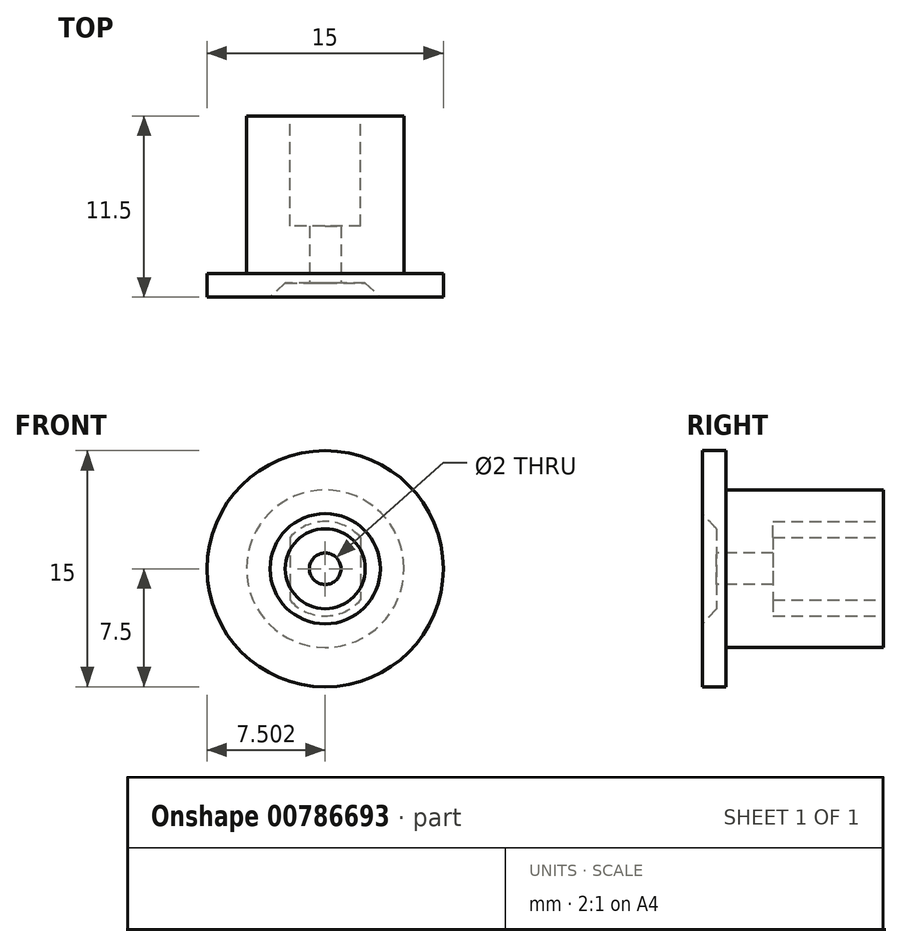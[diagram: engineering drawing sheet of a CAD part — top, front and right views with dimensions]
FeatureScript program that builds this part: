
annotation { "Feature Type Name" : "Feature", "Feature Type Description" : "" }
export const myFeature = defineFeature(function(context is Context, id is Id, definition is map)
    precondition{}
    {
        {
            var Q0;
            Q0=qCreatedBy(makeId("Top.planeOp"),FACE);
            var sketch = newSketch(context, id + "F0", { "sketchPlane" : qUnion([Q0])});
            skLineSegment(sketch, "E0", {"start": v(-45.82, -22.8) * mm, "end": v(-45.82, -33.4) * mm});
            skLineSegment(sketch, "E1", {"start": v(-45.82, -33.4) * mm, "end": v(-48.36, -33.4) * mm});
            skLineSegment(sketch, "E2", {"start": v(-48.36, -33.4) * mm, "end": v(-49.32, -34.3) * mm});
            skLineSegment(sketch, "E3", {"start": v(-49.32, -34.3) * mm, "end": v(-53.32, -34.3) * mm});
            skLineSegment(sketch, "E4", {"start": v(-53.32, -34.3) * mm, "end": v(-53.32, -32.8) * mm});
            skLineSegment(sketch, "E5", {"start": v(-53.32, -32.8) * mm, "end": v(-50.82, -32.8) * mm});
            skLineSegment(sketch, "E6", {"start": v(-50.82, -32.8) * mm, "end": v(-50.82, -22.8) * mm});
            skLineSegment(sketch, "E7", {"start": v(-50.82, -22.8) * mm, "end": v(-45.82, -22.8) * mm});
            skSolve(sketch);
        }
        {
            var Q0;
            Q0=makeQuery(id+"F0.imprint","IMPRINT",FACE,{"disambiguationData":[TD([[makeQuery(id+"F0.imprint","IMPRINT",EDGE,{"derivedFrom":sQuery(id+"F0.wireOp",EDGE,"E0")}),-1.0]])]});
            var Q1;
            Q1=sQuery(id+"F0.wireOp",EDGE,"E0");
            revolve(context, id + "F1", {"surfaceOperationType" : NewSurfaceOperationType.NEW, "entities" : qUnion([Q0]), "axis" : qUnion([Q1]), "revolveType" : RevolveType.FULL});
        }
        {
            var Q0;
            Q0=makeQuery(id+"F1.opRevolve","SWEPT_FACE",FACE,{"disambiguationData":[OSD([sQuery(id+"F0.wireOp",EDGE,"E7")])]});
            var sketch = newSketch(context, id + "F2", { "sketchPlane" : qUnion([Q0])});
            skArc(sketch, "E8", {"start": v(43.57, -1.98) * mm, "mid": v(45.82, -3) * mm, "end": v(48.07, -1.98) * mm});
            skLineSegment(sketch, "E9.bottom", {"start": v(43.57, 9.33) * mm, "end": v(48.07, 9.33) * mm});
            skLineSegment(sketch, "E9.top", {"start": v(43.57, -10.14) * mm, "end": v(48.07, -10.14) * mm});
            skLineSegment(sketch, "E9.left", {"start": v(43.57, 1.98) * mm, "end": v(43.57, -1.98) * mm});
            skLineSegment(sketch, "E9.right", {"start": v(48.07, 1.98) * mm, "end": v(48.07, -1.98) * mm});
            skLineSegment(sketch, "E10", {"start": v(45.82, 0) * mm, "end": v(45.82, -15.12) * mm, "construction": true});
            skArc(sketch, "E11.trimOffspring", {"start": v(48.07, 1.98) * mm, "mid": v(45.82, 3) * mm, "end": v(43.57, 1.98) * mm});
            skSolve(sketch);
        }
        {
            var Q0;
            Q0=makeQuery(id+"F2.imprint","IMPRINT",FACE,{"disambiguationData":[TD([[makeQuery(id+"F2.imprint","IMPRINT",EDGE,{"derivedFrom":sQuery(id+"F2.wireOp",EDGE,"E8")}),1.0]])]});
            extrude(context, id + "F3", {"entities" : qUnion([Q0]), "operationType" : NewBodyOperationType.REMOVE, "oppositeDirection" : true, "depth" : 7 * mm, "offsetDistance" : 25 * mm});
        }
        {
            var Q0;
            Q0=makeQuery(id+"F1.opRevolve","SWEPT_FACE",FACE,{"disambiguationData":[OSD([sQuery(id+"F0.wireOp",EDGE,"E1")])]});
            var sketch = newSketch(context, id + "F4", { "sketchPlane" : qUnion([Q0])});
            skCircle(sketch, "E12", {"center": v(-45.82, 0) * mm, "radius": 1 * mm});
            skSolve(sketch);
        }
        {
            var Q0;
            Q0=makeQuery(id+"F4.imprint","IMPRINT",FACE,{"disambiguationData":[TD([[makeQuery(id+"F4.imprint","IMPRINT",EDGE,{"derivedFrom":sQuery(id+"F4.wireOp",EDGE,"E12")}),1.0]])]});
            extrude(context, id + "F5", {"entities" : qUnion([Q0]), "operationType" : NewBodyOperationType.REMOVE, "oppositeDirection" : true, "depth" : 25 * mm, "offsetDistance" : 25 * mm});
        }
    });
